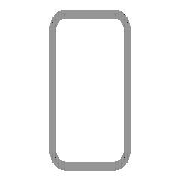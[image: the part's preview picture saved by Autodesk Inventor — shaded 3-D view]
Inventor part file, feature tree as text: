
AUTODESK INVENTOR PART (.ipt)
format: ipt  version: 2025 (Build 290162010, 162A)  size: 129,024 bytes
history: native  units: mm (DEFAULTED — no unit token found)
features: other x3, sketch x1, plane x1
ambient origin geometry x8: Origin, YZ Plane, XZ Plane, XY Plane, X Axis, Y Axis, Z Axis, Center Point
bodies: Solid1 (feature_tree), Body (feature_tree)
feature tree (5):
  other  "Driven Length"
  other  "Start plane"
  other  "End plane"
  sketch  "Sketch3"  dims[d3=2500.0mm d4=0.0mm d7=4.0mm d9=40.0mm d11=80.0mm d12=2.0mm d13=-0.0mm d14=2500.0mm d15=20.0mm d16=40.0mm d17=90.0deg d18=2500.0mm]
  plane  "Work Plane3"
